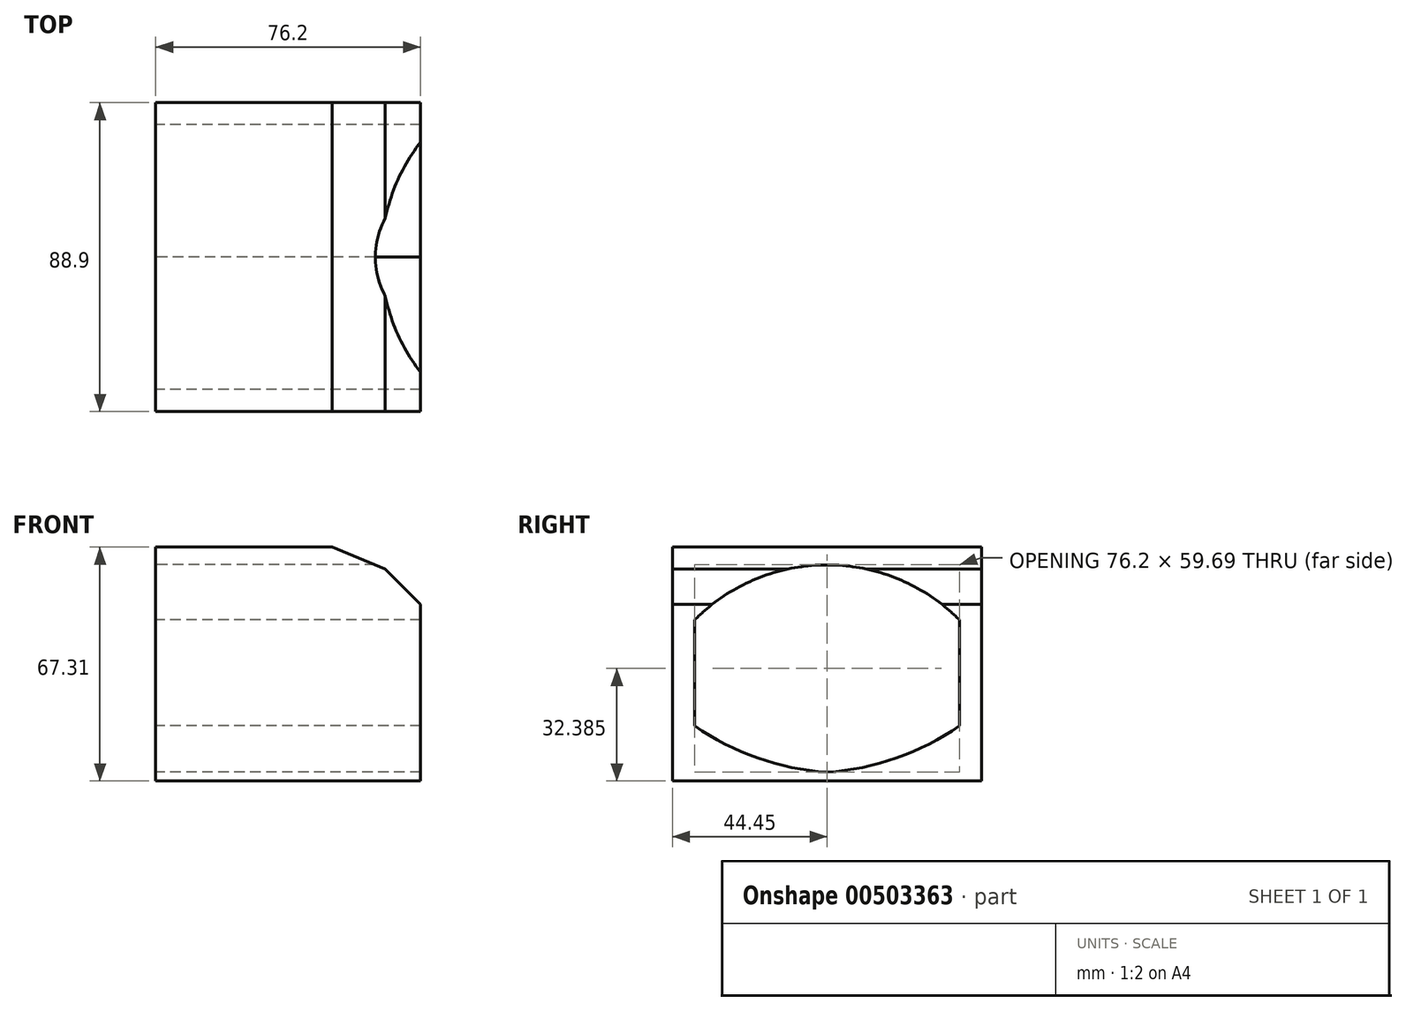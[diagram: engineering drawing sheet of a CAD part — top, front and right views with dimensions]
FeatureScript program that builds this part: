
annotation { "Feature Type Name" : "Feature", "Feature Type Description" : "" }
export const myFeature = defineFeature(function(context is Context, id is Id, definition is map)
    precondition{}
    {
        {
            var Q0;
            Q0=qCreatedBy(makeId("Front.planeOp"),FACE);
            var sketch = newSketch(context, id + "F0", { "sketchPlane" : qUnion([Q0])});
            skLineSegment(sketch, "E0", {"start": v(0, 0) * mm, "end": v(0, 67.31) * mm});
            skLineSegment(sketch, "E1", {"start": v(0, 67.31) * mm, "end": v(50.8, 67.31) * mm});
            skLineSegment(sketch, "E2", {"start": v(50.8, 67.31) * mm, "end": v(66.04, 61.04) * mm});
            skLineSegment(sketch, "E3", {"start": v(76.2, 50.8) * mm, "end": v(76.2, 0) * mm});
            skLineSegment(sketch, "E4", {"start": v(76.2, 0) * mm, "end": v(0, 0) * mm});
            skLineSegment(sketch, "E5", {"start": v(66.04, 61.04) * mm, "end": v(0, 61.04) * mm});
            skLineSegment(sketch, "E6", {"start": v(66.04, 61.04) * mm, "end": v(76.2, 50.8) * mm});
            skSolve(sketch);
        }
        {
            var Q0;
            Q0=makeQuery(id+"F0.imprint","IMPRINT",FACE,{"disambiguationData":[TD([[makeQuery(id+"F0.imprint","IMPRINT",EDGE,{"derivedFrom":sQuery(id+"F0.wireOp",EDGE,"E3")}),-1.0]])]});
            var Q1;
            {var subQ0=sQuery(id+"F0.wireOp",EDGE,"E1");Q1=makeQuery(id+"F0.imprint","IMPRINT",FACE,{"disambiguationData":[TD([[makeQuery(id+"F0.imprint","IMPRINT",EDGE,{"derivedFrom":subQ0}),-1.0]])]});}
            var Q2;
            Q2=sQuery(id+"F0.wireOp",EDGE,"E4");
            var Q3;
            Q3=sQuery(id+"F0.wireOp",EDGE,"E5");
            extrude(context, id + "F1", {"entities" : qUnion([Q0, Q1]), "surfaceEntities" : qUnion([Q2, Q3]), "depth" : 88.9 * mm});
        }
        {
            var Q0;
            Q0=makeQuery(id+"F1.opExtrude","SWEPT_FACE",FACE,{"disambiguationData":[OSD([sQuery(id+"F0.wireOp",EDGE,"E0")])]});
            var sketch = newSketch(context, id + "F2", { "sketchPlane" : qUnion([Q0])});
            skLineSegment(sketch, "E7", {"start": v(44.45, 0) * mm, "end": v(44.45, 2.54) * mm});
            skPoint(sketch, "E7.endSnap0", {"position": v(44.45, 0) * mm});
            skLineSegment(sketch, "E8", {"start": v(0, 33.66) * mm, "end": v(6.35, 33.66) * mm});
            skPoint(sketch, "E8.endSnap0", {"position": v(0, 33.66) * mm});
            skLineSegment(sketch, "E9", {"start": v(88.9, 33.66) * mm, "end": v(82.55, 33.66) * mm});
            skPoint(sketch, "E9.endSnap0", {"position": v(88.9, 33.66) * mm});
            skLineSegment(sketch, "E10", {"start": v(44.45, 0) * mm, "end": v(44.45, -14.22) * mm});
            skLineSegment(sketch, "E11", {"start": v(44.45, 67.31) * mm, "end": v(44.45, 62.23) * mm});
            skPoint(sketch, "E11.endSnap0", {"position": v(44.45, 67.31) * mm});
            skLineSegment(sketch, "E12", {"start": v(6.35, 33.66) * mm, "end": v(6.35, 15.88) * mm});
            skLineSegment(sketch, "E13", {"start": v(6.35, 33.66) * mm, "end": v(6.35, 46.36) * mm});
            skLineSegment(sketch, "E14", {"start": v(82.55, 33.66) * mm, "end": v(82.55, 46.36) * mm});
            skLineSegment(sketch, "E15", {"start": v(82.55, 33.66) * mm, "end": v(82.55, 15.88) * mm});
            skArc(sketch, "E16", {"start": v(6.35, 15.87) * mm, "mid": v(24.5, 6.64) * mm, "end": v(44.45, 2.54) * mm});
            skArc(sketch, "E17", {"start": v(44.45, 2.54) * mm, "mid": v(64.4, 6.64) * mm, "end": v(82.55, 15.88) * mm});
            skArc(sketch, "E18", {"start": v(82.55, 46.36) * mm, "mid": v(44.45, 62.23) * mm, "end": v(6.35, 46.36) * mm});
            skSolve(sketch);
        }
        {
            var Q0;
            Q0=makeQuery(id+"F2.imprint","IMPRINT",FACE,{"disambiguationData":[TD([[makeQuery(id+"F2.imprint","IMPRINT",EDGE,{"derivedFrom":sQuery(id+"F2.wireOp",EDGE,"E12")}),1.0]])]});
            extrude(context, id + "F3", {"entities" : qUnion([Q0]), "operationType" : NewBodyOperationType.REMOVE, "endBound" : BoundingType.THROUGH_ALL, "oppositeDirection" : true, "depth" : 25.4 * mm});
        }
    });
